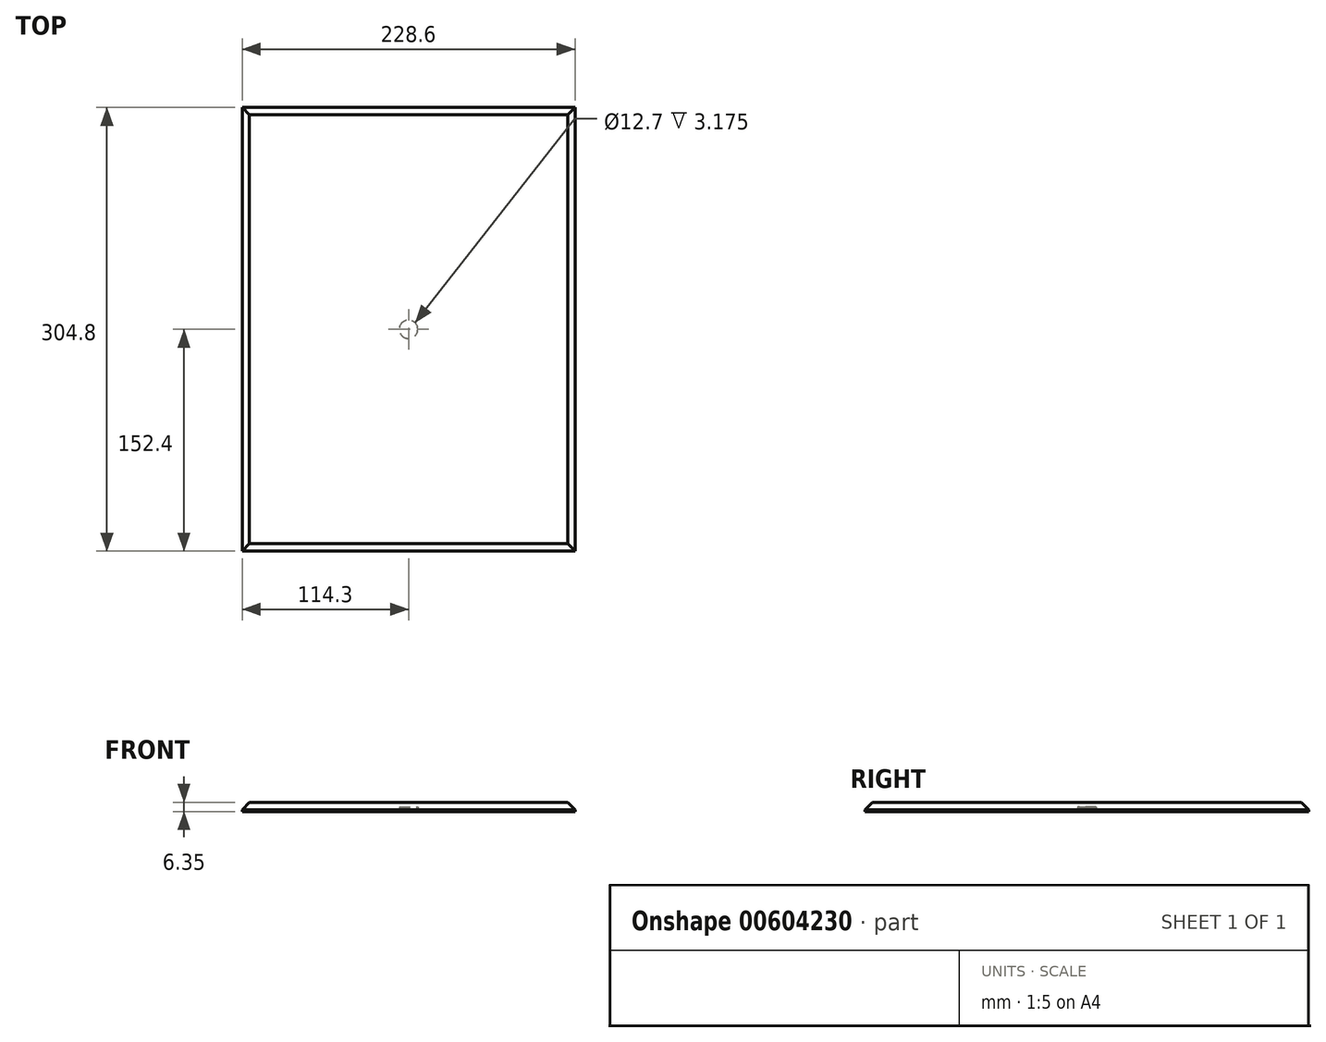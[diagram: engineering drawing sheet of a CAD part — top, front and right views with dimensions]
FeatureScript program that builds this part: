
annotation { "Feature Type Name" : "Feature", "Feature Type Description" : "" }
export const myFeature = defineFeature(function(context is Context, id is Id, definition is map)
    precondition{}
    {
        {
            var Q0;
            Q0=qCreatedBy(makeId("Top.planeOp"),FACE);
            var sketch = newSketch(context, id + "F0", { "sketchPlane" : qUnion([Q0])});
            skLineSegment(sketch, "E0.bottom", {"start": v(114.3, 152.4) * mm, "end": v(-114.3, 152.4) * mm});
            skLineSegment(sketch, "E0.top", {"start": v(114.3, -152.4) * mm, "end": v(-114.3, -152.4) * mm});
            skLineSegment(sketch, "E0.left", {"start": v(114.3, 152.4) * mm, "end": v(114.3, -152.4) * mm});
            skLineSegment(sketch, "E0.right", {"start": v(-114.3, 152.4) * mm, "end": v(-114.3, -152.4) * mm});
            skPoint(sketch, "E0.middle", {"position": v(0, 0) * mm});
            skSolve(sketch);
        }
        {
            var Q0;
            Q0=makeQuery(id+"F0.imprint","IMPRINT",FACE,{"disambiguationData":[TD([[makeQuery(id+"F0.imprint","IMPRINT",EDGE,{"derivedFrom":sQuery(id+"F0.wireOp",EDGE,"E0.bottom")}),1.0]])]});
            extrude(context, id + "F1", {"entities" : qUnion([Q0]), "depth" : 6.35 * mm, "offsetDistance" : 25.4 * mm});
        }
        {
            var Q0;
            Q0=makeQuery(id+"F1.opExtrude","CAP_FACE",FACE,{"disambiguationData":[OSD([sQuery(id+"F0.wireOp",EDGE,"E0.bottom"),sQuery(id+"F0.wireOp",EDGE,"E0.top"),sQuery(id+"F0.wireOp",EDGE,"E0.left"),sQuery(id+"F0.wireOp",EDGE,"E0.right")])],"isStart":true});
            var sketch = newSketch(context, id + "F2", { "sketchPlane" : qUnion([Q0])});
            skCircle(sketch, "E1", {"center": v(0, 0) * mm, "radius": 6.35 * mm});
            skSolve(sketch);
        }
        {
            var Q0;
            Q0=makeQuery(id+"F2.imprint","IMPRINT",FACE,{"disambiguationData":[TD([[makeQuery(id+"F2.imprint","IMPRINT",EDGE,{"derivedFrom":sQuery(id+"F2.wireOp",EDGE,"E1")}),1.0]])]});
            extrude(context, id + "F3", {"entities" : qUnion([Q0]), "operationType" : NewBodyOperationType.REMOVE, "oppositeDirection" : true, "depth" : 3.17 * mm, "offsetDistance" : 25.4 * mm});
        }
        {
            var Q0;
            Q0=makeQuery(id+"F1.opExtrude","CAP_EDGE",EDGE,{"disambiguationData":[OSD([sQuery(id+"F0.wireOp",EDGE,"E0.right")])],"isStart":false});
            var Q1;
            Q1=makeQuery(id+"F1.opExtrude","CAP_EDGE",EDGE,{"disambiguationData":[OSD([sQuery(id+"F0.wireOp",EDGE,"E0.bottom")])],"isStart":false});
            var Q2;
            Q2=makeQuery(id+"F1.opExtrude","CAP_EDGE",EDGE,{"disambiguationData":[OSD([sQuery(id+"F0.wireOp",EDGE,"E0.left")])],"isStart":false});
            var Q3;
            Q3=makeQuery(id+"F1.opExtrude","CAP_EDGE",EDGE,{"disambiguationData":[OSD([sQuery(id+"F0.wireOp",EDGE,"E0.top")])],"isStart":false});
            chamfer(context, id + "F4", {"entities" : qUnion([Q0, Q1, Q2, Q3]), "width" : 5.08 * mm, "tangentPropagation" : true});
        }
    });
